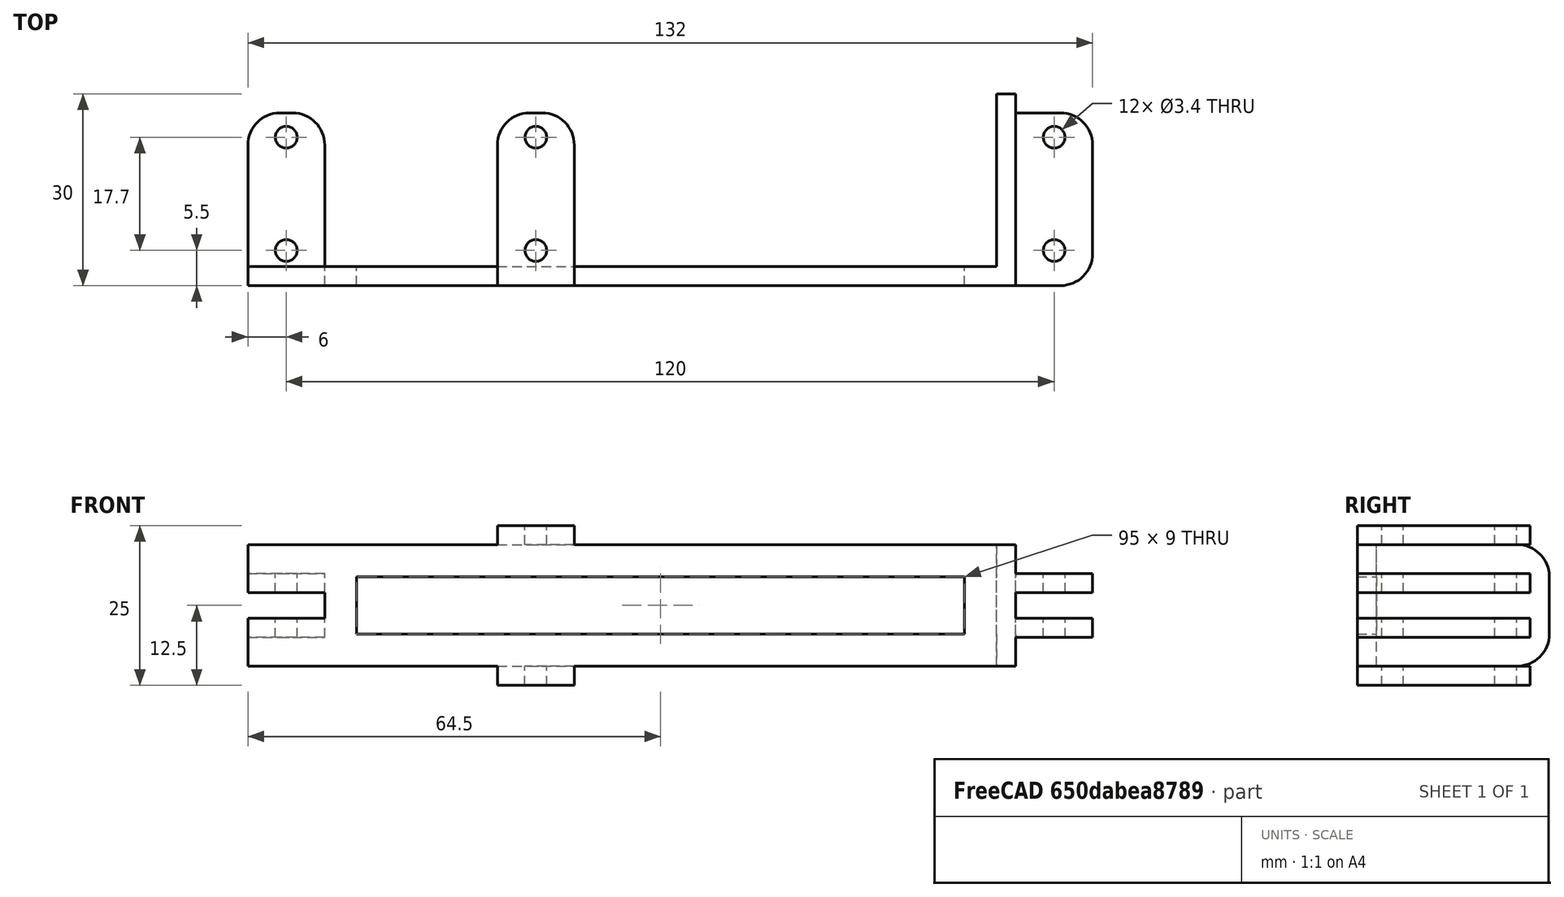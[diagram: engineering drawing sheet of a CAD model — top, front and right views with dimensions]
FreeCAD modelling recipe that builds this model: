
FCSTD DOCUMENT  (FreeCAD 0.15R4671 (Git))
Label: runner base3
License: CreativeCommons Attribution-ShareAlike
LicenseURL: http://creativecommons.org/licenses/by-sa/4.0/
objects: Part::Box×10, Part::MultiFuse×5, Part::Cut×3, Part::Cylinder×2, Part::Fillet×1
note: 21 computed .brp shape members not serialized (recipe doc carries the construction recipe); baked Part::Feature solids carry a one-line shape summary decoded from their .brp

FEATURE [Part::Box] Box  label="Cube"
  Height = 19
  Length = 117
  Placement = pos=(-39,0,0) rot=(0,0,1;0rad)
  Width = 3
FEATURE [Part::Box] Box001  label="Cube001"
  Height = 3
  Length = 12
  Placement = pos=(0,0,-3) rot=(0,0,1;0rad)
  Width = 27
FEATURE [Part::Box] Box002  label="Cube002"
  Height = 3
  Length = 12
  Placement = pos=(0,0,19) rot=(0,0,1;0rad)
  Width = 27
FEATURE [Part::Box] Box003  label="Cube003"
  Height = 19
  Length = 3
  Placement = pos=(78,0,0) rot=(0,0,1;0rad)
  Width = 30
FEATURE [Part::Cylinder] Cylinder
  Angle = 360
  Height = 31
  Placement = pos=(6,5.5,-6) rot=(0,0,1;0rad)
  Radius = 1.7
FEATURE [Part::Cylinder] Cylinder001
  Angle = 360
  Height = 31
  Placement = pos=(6,23.2,-6) rot=(0,0,1;0rad)
  Radius = 1.7
FEATURE [Part::Box] Box004  label="Cube004"
  Height = 3
  Length = 12
  Placement = pos=(-39,0,4.5) rot=(0,0,1;0rad)
  Width = 27
FEATURE [Part::Box] Box005  label="Cube005"
  Height = 3
  Length = 12
  Placement = pos=(-39,0,11.5) rot=(0,0,1;0rad)
  Width = 27
FEATURE [Part::Box] Box006  label="Cube006"
  Height = 3
  Length = 12
  Placement = pos=(81,0,4.5) rot=(0,0,1;0rad)
  Width = 27
FEATURE [Part::Box] Box007  label="Cube007"
  Height = 3
  Length = 12
  Placement = pos=(81,0,11.5) rot=(0,0,1;0rad)
  Width = 27
FEATURE [Part::MultiFuse] Fusion001
  Shapes = -> [Cylinder,Cylinder001]
FEATURE [Part::MultiFuse] Fusion002
  Placement = pos=(81,0,0) rot=(0,0,1;0rad)
  Shapes = -> [Cylinder,Cylinder001]
FEATURE [Part::MultiFuse] Fusion003
  Placement = pos=(-39,0,0) rot=(0,0,1;0rad)
  Shapes = -> [Cylinder,Cylinder001]
FEATURE [Part::MultiFuse] Fusion004  label="cilindros"
  Shapes = -> [Fusion001,Fusion002,Fusion003]
FEATURE [Part::Box] Box008  label="Cube008"
  Height = 4
  Length = 12
  Placement = pos=(-39,-7,7.5) rot=(0,0,1;0rad)
  Width = 10
FEATURE [Part::Cut] Cut
  Base = -> Box
  Tool = -> Box008
FEATURE [Part::MultiFuse] Fusion
  Shapes = -> [Box004,Box005,Box006,Box007,Box003,Box001,Box002,Cut]
FEATURE [Part::Cut] Cut001
  Base = -> Fusion
  Tool = -> Fusion004
FEATURE [Part::Fillet] Fillet
  Base = -> Cut001
  Edges = 14 edges r=5: [Edge29,Edge32,Edge42,Edge51,Edge58,Edge60,Edge67,Edge73,Edge89,Edge97,Edge103,Edge105,Edge128,Edge132]
FEATURE [Part::Box] Box009  label="Cube009"
  Height = 9
  Length = 95
  Placement = pos=(-22,0,5) rot=(0,0,1;0rad)
  Width = 5
FEATURE [Part::Cut] Cut002
  Base = -> Fillet
  Tool = -> Box009
